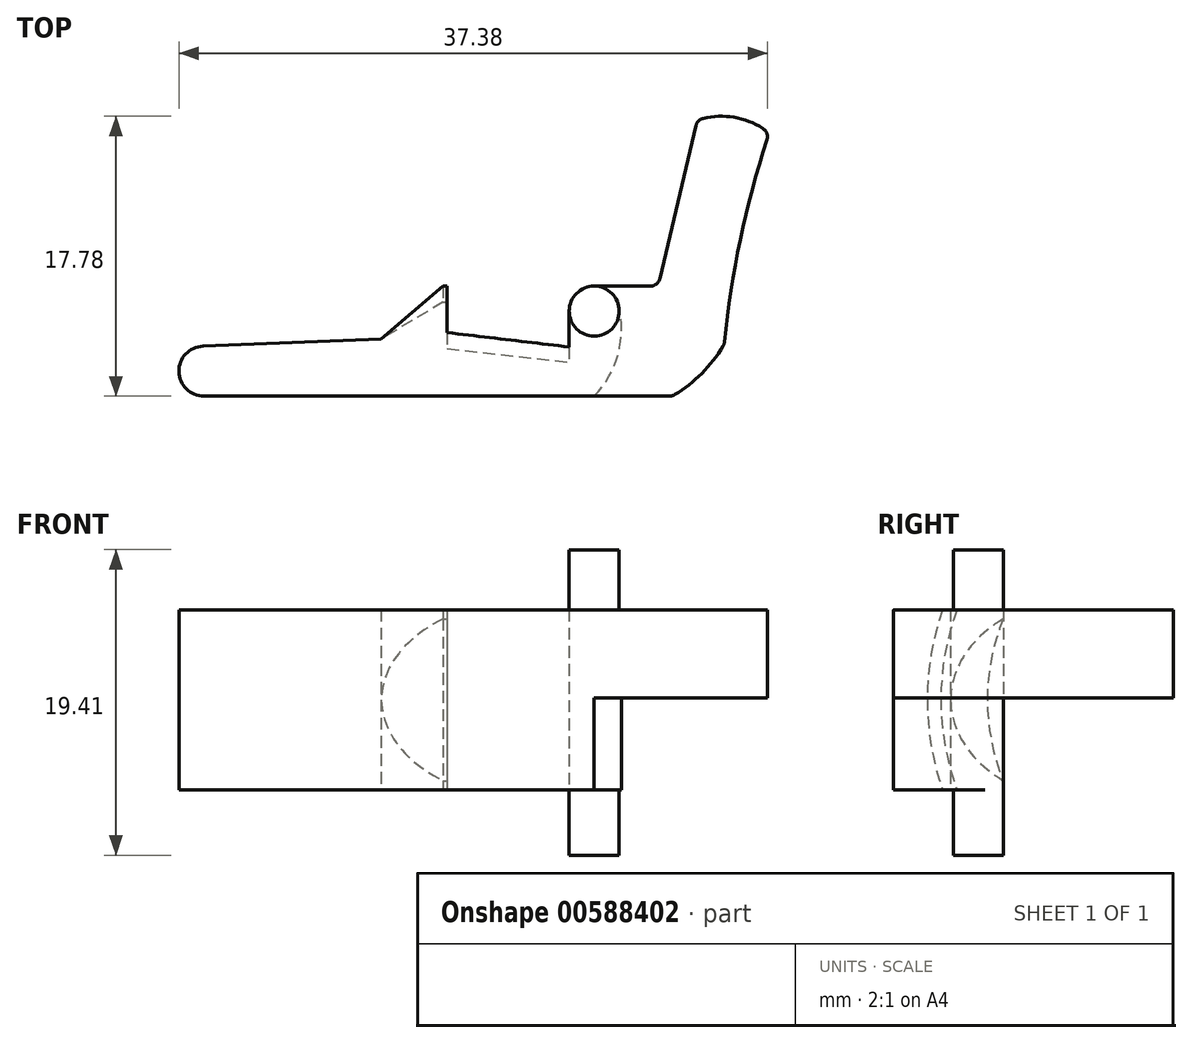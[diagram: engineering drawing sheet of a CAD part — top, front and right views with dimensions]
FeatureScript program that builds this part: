
annotation { "Feature Type Name" : "Feature", "Feature Type Description" : "" }
export const myFeature = defineFeature(function(context is Context, id is Id, definition is map)
    precondition{}
    {
        {
            var Q0;
            Q0=qCreatedBy(makeId("Top.planeOp"),FACE);
            var sketch = newSketch(context, id + "F0", { "sketchPlane" : qUnion([Q0])});
            skArc(sketch, "E0", {"start": v(0, 1.59) * mm, "mid": v(-1.12, 1.12) * mm, "end": v(-1.59, 0) * mm});
            skLineSegment(sketch, "E1", {"start": v(-1.59, 0) * mm, "end": v(-1.59, -2.22) * mm});
            skLineSegment(sketch, "E2", {"start": v(0, 1.59) * mm, "end": v(-19.22, 1.59) * mm, "construction": true});
            skLineSegment(sketch, "E3", {"start": v(-1.59, -2.22) * mm, "end": v(-9.33, -1.36) * mm});
            skLineSegment(sketch, "E4", {"start": v(-9.33, -1.36) * mm, "end": v(-9.33, 1.59) * mm});
            skLineSegment(sketch, "E5", {"start": v(-9.33, 1.59) * mm, "end": v(-9.6, 1.59) * mm});
            skPoint(sketch, "E5.endSnap0", {"position": v(-9.6, 1.59) * mm});
            skLineSegment(sketch, "E6", {"start": v(-9.6, 1.59) * mm, "end": v(-13.53, -1.77) * mm});
            skLineSegment(sketch, "E7", {"start": v(-1.59, -2.22) * mm, "end": v(-26.19, -2.22) * mm, "construction": true});
            skLineSegment(sketch, "E8", {"start": v(-13.53, -1.77) * mm, "end": v(-24.85, -2.22) * mm});
            skArc(sketch, "E9", {"start": v(-24.73, -2.22) * mm, "mid": v(-26.38, -3.78) * mm, "end": v(-24.79, -5.4) * mm});
            skLineSegment(sketch, "E10", {"start": v(-24.79, -5.4) * mm, "end": v(4.78, -5.4) * mm});
            skArc(sketch, "E11", {"start": v(10.71, 11.6) * mm, "mid": v(8.88, 12.31) * mm, "end": v(6.92, 12.25) * mm});
            skLineSegment(sketch, "E12", {"start": v(8.07, 12.38) * mm, "end": v(-7.67, 12.38) * mm, "construction": true});
            skPoint(sketch, "E12.startSnap0", {"position": v(8.07, 12.38) * mm});
            skArc(sketch, "E13", {"start": v(5.1, -5.3) * mm, "mid": v(6.83, -3.95) * mm, "end": v(8.18, -2.22) * mm});
            skArc(sketch, "E14", {"start": v(10.97, 10.89) * mm, "mid": v(9.27, 4.54) * mm, "end": v(8.27, -1.96) * mm});
            skLineSegment(sketch, "E15", {"start": v(11.11, 11.32) * mm, "end": v(11.11, -5.8) * mm, "construction": true});
            skPoint(sketch, "E16.visualSharp", {"position": v(11.11, 11.32) * mm});
            skArc(sketch, "E16.filletArc", {"start": v(10.97, 10.89) * mm, "mid": v(10.96, 11.3) * mm, "end": v(10.71, 11.6) * mm});
            skLineSegment(sketch, "E17", {"start": v(6.54, 12.14) * mm, "end": v(6.54, 16.1) * mm, "construction": true});
            skLineSegment(sketch, "E18", {"start": v(0, 1.59) * mm, "end": v(3.55, 1.59) * mm});
            skLineSegment(sketch, "E19", {"start": v(6.46, 11.78) * mm, "end": v(4.17, 2.07) * mm});
            skPoint(sketch, "E20.visualSharp", {"position": v(4.05, 1.59) * mm});
            skArc(sketch, "E20.filletArc", {"start": v(3.55, 1.59) * mm, "mid": v(3.94, 1.72) * mm, "end": v(4.17, 2.07) * mm});
            skPoint(sketch, "E21.visualSharp", {"position": v(8.25, -2.1) * mm});
            skArc(sketch, "E21.filletArc", {"start": v(8.18, -2.22) * mm, "mid": v(8.24, -2.1) * mm, "end": v(8.27, -1.96) * mm});
            skPoint(sketch, "E22.visualSharp", {"position": v(4.96, -5.4) * mm});
            skArc(sketch, "E22.filletArc", {"start": v(4.78, -5.4) * mm, "mid": v(4.95, -5.37) * mm, "end": v(5.1, -5.3) * mm});
            skPoint(sketch, "E23.visualSharp", {"position": v(6.54, 12.14) * mm});
            skArc(sketch, "E23.filletArc", {"start": v(6.92, 12.25) * mm, "mid": v(6.62, 12.08) * mm, "end": v(6.46, 11.78) * mm});
            skSolve(sketch);
        }
        {
            var Q0;
            Q0 = qSketchRegion(id + "F0", true);
            extrude(context, id + "F1", {"entities" : qUnion([Q0]), "endBound" : BoundingType.SYMMETRIC, "depth" : 11.43 * mm, "offsetDistance" : 25.4 * mm});
        }
        {
            var Q0;
            Q0=makeQuery(id+"F1.opExtrude","CAP_FACE",FACE,{"disambiguationData":[OSD([sQuery(id+"F0.wireOp",EDGE,"E0"),sQuery(id+"F0.wireOp",EDGE,"E1"),sQuery(id+"F0.wireOp",EDGE,"E3"),sQuery(id+"F0.wireOp",EDGE,"E4"),sQuery(id+"F0.wireOp",EDGE,"E5"),sQuery(id+"F0.wireOp",EDGE,"E6"),sQuery(id+"F0.wireOp",EDGE,"E8"),sQuery(id+"F0.wireOp",EDGE,"E9"),sQuery(id+"F0.wireOp",EDGE,"E10"),sQuery(id+"F0.wireOp",EDGE,"E11"),sQuery(id+"F0.wireOp",EDGE,"E13"),sQuery(id+"F0.wireOp",EDGE,"E14"),sQuery(id+"F0.wireOp",EDGE,"E16.filletArc"),sQuery(id+"F0.wireOp",EDGE,"E18"),sQuery(id+"F0.wireOp",EDGE,"E19"),sQuery(id+"F0.wireOp",EDGE,"E20.filletArc"),sQuery(id+"F0.wireOp",EDGE,"E21.filletArc"),sQuery(id+"F0.wireOp",EDGE,"E22.filletArc"),sQuery(id+"F0.wireOp",EDGE,"E23.filletArc")])],"isStart":true});
            var sketch = newSketch(context, id + "F2", { "sketchPlane" : qUnion([Q0])});
            skCircle(sketch, "E24", {"center": v(0, 0) * mm, "radius": 1.59 * mm});
            skSolve(sketch);
        }
        {
            var Q0;
            Q0 = qSketchRegion(id + "F2", true);
            extrude(context, id + "F3", {"entities" : qUnion([Q0]), "operationType" : NewBodyOperationType.ADD, "depth" : 4.17 * mm, "offsetDistance" : 25.4 * mm});
        }
        {
            var Q0;
            Q0=makeQuery(id+"F1.opExtrude","CAP_FACE",FACE,{"disambiguationData":[OSD([sQuery(id+"F0.wireOp",EDGE,"E0"),sQuery(id+"F0.wireOp",EDGE,"E1"),sQuery(id+"F0.wireOp",EDGE,"E3"),sQuery(id+"F0.wireOp",EDGE,"E4"),sQuery(id+"F0.wireOp",EDGE,"E5"),sQuery(id+"F0.wireOp",EDGE,"E6"),sQuery(id+"F0.wireOp",EDGE,"E8"),sQuery(id+"F0.wireOp",EDGE,"E9"),sQuery(id+"F0.wireOp",EDGE,"E10"),sQuery(id+"F0.wireOp",EDGE,"E11"),sQuery(id+"F0.wireOp",EDGE,"E13"),sQuery(id+"F0.wireOp",EDGE,"E14"),sQuery(id+"F0.wireOp",EDGE,"E16.filletArc"),sQuery(id+"F0.wireOp",EDGE,"E18"),sQuery(id+"F0.wireOp",EDGE,"E19"),sQuery(id+"F0.wireOp",EDGE,"E20.filletArc"),sQuery(id+"F0.wireOp",EDGE,"E21.filletArc"),sQuery(id+"F0.wireOp",EDGE,"E22.filletArc"),sQuery(id+"F0.wireOp",EDGE,"E23.filletArc")])],"isStart":false});
            var sketch = newSketch(context, id + "F4", { "sketchPlane" : qUnion([Q0])});
            skCircle(sketch, "E25", {"center": v(0, 0) * mm, "radius": 1.59 * mm});
            skSolve(sketch);
        }
        {
            var Q0;
            Q0 = qSketchRegion(id + "F4", true);
            extrude(context, id + "F5", {"entities" : qUnion([Q0]), "operationType" : NewBodyOperationType.ADD, "depth" : 3.8 * mm, "offsetDistance" : 25.4 * mm});
        }
        {
            var Q0;
            Q0=makeQuery(id+"F1.opExtrude","CAP_FACE",FACE,{"disambiguationData":[OSD([sQuery(id+"F0.wireOp",EDGE,"E0"),sQuery(id+"F0.wireOp",EDGE,"E1"),sQuery(id+"F0.wireOp",EDGE,"E3"),sQuery(id+"F0.wireOp",EDGE,"E4"),sQuery(id+"F0.wireOp",EDGE,"E5"),sQuery(id+"F0.wireOp",EDGE,"E6"),sQuery(id+"F0.wireOp",EDGE,"E8"),sQuery(id+"F0.wireOp",EDGE,"E9"),sQuery(id+"F0.wireOp",EDGE,"E10"),sQuery(id+"F0.wireOp",EDGE,"E11"),sQuery(id+"F0.wireOp",EDGE,"E13"),sQuery(id+"F0.wireOp",EDGE,"E14"),sQuery(id+"F0.wireOp",EDGE,"E16.filletArc"),sQuery(id+"F0.wireOp",EDGE,"E18"),sQuery(id+"F0.wireOp",EDGE,"E19"),sQuery(id+"F0.wireOp",EDGE,"E20.filletArc"),sQuery(id+"F0.wireOp",EDGE,"E21.filletArc"),sQuery(id+"F0.wireOp",EDGE,"E22.filletArc"),sQuery(id+"F0.wireOp",EDGE,"E23.filletArc")])],"isStart":true});
            var sketch = newSketch(context, id + "F6", { "sketchPlane" : qUnion([Q0])});
            skLineSegment(sketch, "E26", {"start": v(0, -1.59) * mm, "end": v(0, -1.59) * mm});
            skLineSegment(sketch, "E27", {"start": v(0, 5.4) * mm, "end": v(9.2, 17.43) * mm});
            skLineSegment(sketch, "E28", {"start": v(9.2, 17.43) * mm, "end": v(23.12, -22.88) * mm});
            skLineSegment(sketch, "E29", {"start": v(23.12, -22.88) * mm, "end": v(-3.65, -20.05) * mm});
            skLineSegment(sketch, "E30", {"start": v(-3.65, -20.05) * mm, "end": v(0, -1.59) * mm});
            skArc(sketch, "E31.0", {"start": v(0, -1.59) * mm, "mid": v(0.97, -1.26) * mm, "end": v(1.54, -0.4) * mm});
            skArc(sketch, "E32", {"start": v(1.54, -0.4) * mm, "mid": v(1.53, 2.7) * mm, "end": v(0, 5.4) * mm});
            skPoint(sketch, "E33.orphan", {"position": v(-1.59, 0) * mm});
            skSolve(sketch);
        }
        {
            var Q0;
            Q0 = qSketchRegion(id + "F6", true);
            extrude(context, id + "F7", {"entities" : qUnion([Q0]), "operationType" : NewBodyOperationType.REMOVE, "oppositeDirection" : true, "depth" : 5.84 * mm, "offsetDistance" : 25.4 * mm});
        }
        {
            var Q0;
            Q0=qCreatedBy(makeId("Top.planeOp"),FACE);
            var sketch = newSketch(context, id + "F8", { "sketchPlane" : qUnion([Q0])});
            skLineSegment(sketch, "E34", {"start": v(-1.59, -3.24) * mm, "end": v(-9.33, -2.38) * mm});
            skLineSegment(sketch, "E35", {"start": v(-13.53, -1.77) * mm, "end": v(-13.49, 2.33) * mm});
            skLineSegment(sketch, "E36", {"start": v(-13.49, 2.33) * mm, "end": v(-1.59, 2.22) * mm});
            skLineSegment(sketch, "E37", {"start": v(-1.59, 2.22) * mm, "end": v(-1.59, -3.24) * mm});
            skLineSegment(sketch, "E38", {"start": v(-11.24, 0.57) * mm, "end": v(-13.36, 0.57) * mm, "construction": true});
            skLineSegment(sketch, "E39", {"start": v(-13.53, -1.77) * mm, "end": v(-9.6, 0.57) * mm});
            skLineSegment(sketch, "E40", {"start": v(-9.6, 0.57) * mm, "end": v(-9.33, 0.57) * mm});
            skLineSegment(sketch, "E41", {"start": v(-9.33, 0.57) * mm, "end": v(-9.33, -2.38) * mm});
            skLineSegment(sketch, "E42", {"start": v(-24.44, 14.1) * mm, "end": v(24.9, 14.1) * mm, "construction": true});
            skSolve(sketch);
        }
        {
            var Q0;
            Q0=makeQuery(id+"F8.imprint","IMPRINT",FACE,{"disambiguationData":[TD([[makeQuery(id+"F8.imprint","IMPRINT",EDGE,{"derivedFrom":sQuery(id+"F8.wireOp",EDGE,"E34")}),-1.0]])]});
            var Q1;
            Q1=sQuery(id+"F8.wireOp",EDGE,"E42");
            revolve(context, id + "F9", {"operationType" : NewBodyOperationType.REMOVE, "entities" : qUnion([Q0]), "axis" : qUnion([Q1]), "revolveType" : RevolveType.FULL, "oppositeDirection" : true});
        }
    });
